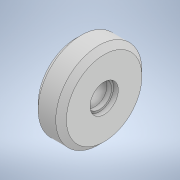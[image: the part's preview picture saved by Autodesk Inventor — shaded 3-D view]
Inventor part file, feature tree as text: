
AUTODESK INVENTOR PART (.ipt)
format: ipt  version: 2022 (Build 260153000, 153)  size: 123,392 bytes
history: native  units: mm
features: sketch x2, other x1, revolve x1, hole x1
ambient origin geometry x8: Origin, YZ Plane, XZ Plane, XY Plane, X Axis, Y Axis, Z Axis, Center Point
bodies: Body1 (feature_tree)
feature tree (5):
  other  "Твердое тело1"
  revolve  "Вращение1"
  hole  "Отверстие1"  [1 undecoded]
  sketch  "Эскиз1"
  sketch  "Эскиз2"
note: 1 required parameter value undecoded (feature->parameter linkage not recoverable at this tier; creation-order binding heuristic only, values carry confidence <= 0.55)
